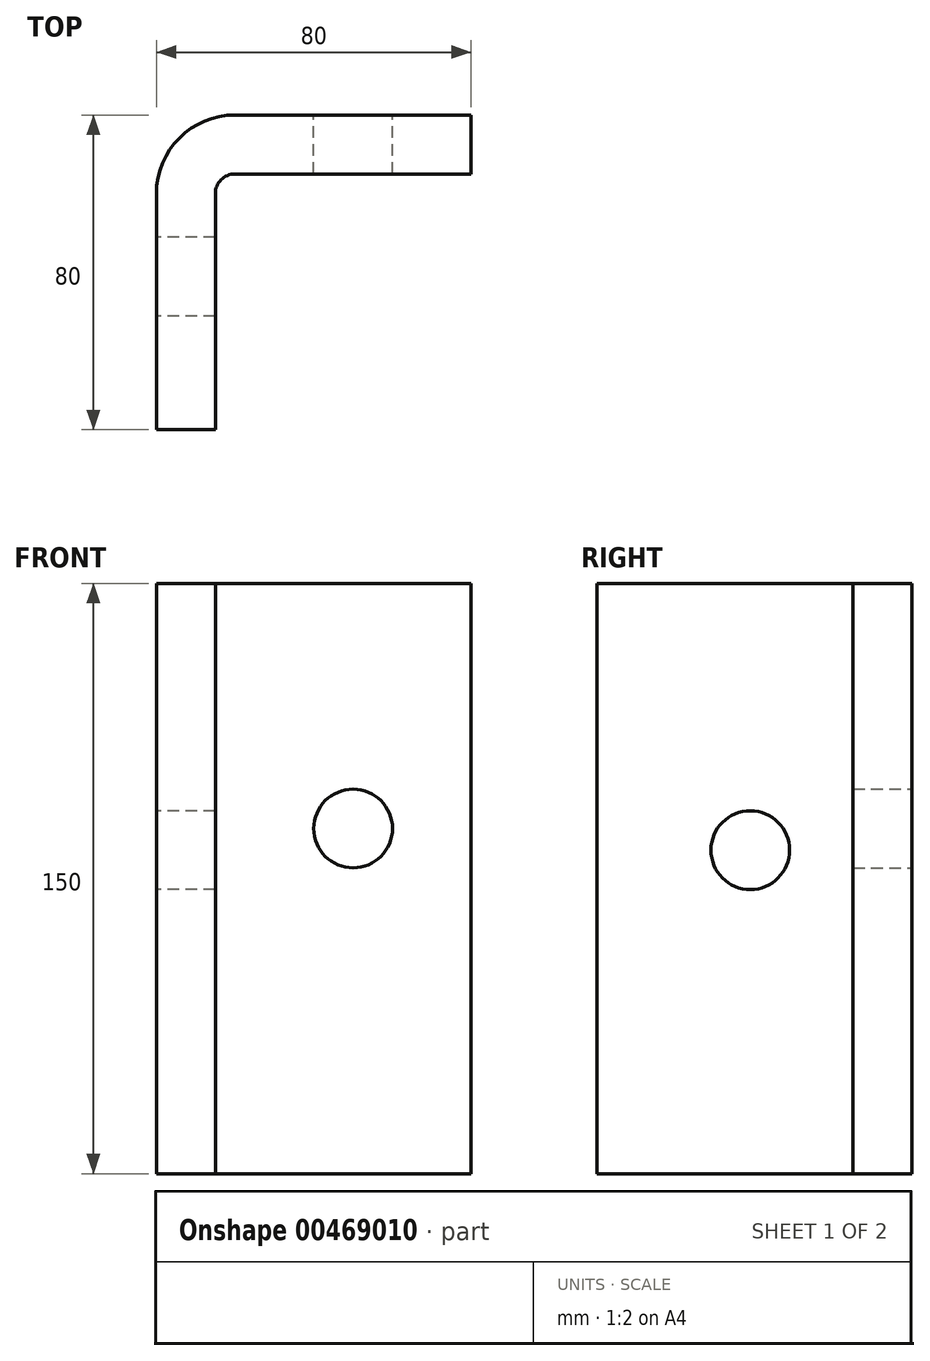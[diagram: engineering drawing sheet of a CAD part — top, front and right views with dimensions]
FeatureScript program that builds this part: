
annotation { "Feature Type Name" : "Feature", "Feature Type Description" : "" }
export const myFeature = defineFeature(function(context is Context, id is Id, definition is map)
    precondition{}
    {
        {
            var Q0;
            Q0=qCreatedBy(makeId("Top.planeOp"),FACE);
            var sketch = newSketch(context, id + "F0", { "sketchPlane" : qUnion([Q0])});
            skLineSegment(sketch, "E0", {"start": v(0, 0) * mm, "end": v(0, 80) * mm});
            skLineSegment(sketch, "E1", {"start": v(0, 80) * mm, "end": v(80, 80) * mm});
            skLineSegment(sketch, "E2", {"start": v(80, 80) * mm, "end": v(80, 65) * mm});
            skLineSegment(sketch, "E3", {"start": v(80, 65) * mm, "end": v(15, 65) * mm});
            skLineSegment(sketch, "E4", {"start": v(15, 65) * mm, "end": v(15, 0) * mm});
            skLineSegment(sketch, "E5", {"start": v(15, 0) * mm, "end": v(0, 0) * mm});
            skSolve(sketch);
        }
        {
            var Q0;
            Q0=makeQuery(id+"F0.imprint","IMPRINT",FACE,{"disambiguationData":[TD([[makeQuery(id+"F0.imprint","IMPRINT",EDGE,{"derivedFrom":sQuery(id+"F0.wireOp",EDGE,"E0")}),-1.0]])]});
            extrude(context, id + "F1", {"entities" : qUnion([Q0]), "depth" : 150 * mm});
        }
        {
            var Q0;
            Q0=makeQuery(id+"F1.opExtrude","SWEPT_EDGE",EDGE,{"disambiguationData":[OSD([sQuery(id+"F0.wireOp",EDGE,"E0"),sQuery(id+"F0.wireOp",EDGE,"E1")])]});
            fillet(context, id + "F2", {"entities" : qUnion([Q0]), "radius" : 20 * mm, "tangentPropagation" : true, "allowEdgeOverflow" : false});
        }
        {
            var Q0;
            Q0=makeQuery(id+"F1.opExtrude","SWEPT_EDGE",EDGE,{"disambiguationData":[OSD([sQuery(id+"F0.wireOp",EDGE,"E3"),sQuery(id+"F0.wireOp",EDGE,"E4")])]});
            fillet(context, id + "F3", {"entities" : qUnion([Q0]), "radius" : 5 * mm, "tangentPropagation" : true, "allowEdgeOverflow" : false});
        }
        {
            var Q0;
            Q0=makeQuery(id+"F1.opExtrude","SWEPT_FACE",FACE,{"disambiguationData":[OSD([sQuery(id+"F0.wireOp",EDGE,"E0")])]});
            var sketch = newSketch(context, id + "F4", { "sketchPlane" : qUnion([Q0])});
            skCircle(sketch, "E6", {"center": v(-38.9, 82.2) * mm, "radius": 10 * mm});
            skSolve(sketch);
        }
        {
            var Q0;
            Q0=makeQuery(id+"F4.imprint","IMPRINT",FACE,{"disambiguationData":[TD([[makeQuery(id+"F4.imprint","IMPRINT",EDGE,{"derivedFrom":sQuery(id+"F4.wireOp",EDGE,"E6")}),1.0]])]});
            extrude(context, id + "F5", {"entities" : qUnion([Q0]), "operationType" : NewBodyOperationType.REMOVE, "endBound" : BoundingType.THROUGH_ALL, "oppositeDirection" : true, "depth" : 25 * mm});
        }
        {
            var Q0;
            Q0=makeQuery(id+"F1.opExtrude","SWEPT_FACE",FACE,{"disambiguationData":[OSD([sQuery(id+"F0.wireOp",EDGE,"E1")])]});
            var sketch = newSketch(context, id + "F6", { "sketchPlane" : qUnion([Q0])});
            skCircle(sketch, "E7", {"center": v(-50, 87.69) * mm, "radius": 10 * mm});
            skPoint(sketch, "E7.centerSnap0", {"position": v(-50, 150) * mm});
            skSolve(sketch);
        }
        {
            var Q0;
            Q0=makeQuery(id+"F6.imprint","IMPRINT",FACE,{"disambiguationData":[TD([[makeQuery(id+"F6.imprint","IMPRINT",EDGE,{"derivedFrom":sQuery(id+"F6.wireOp",EDGE,"E7")}),1.0]])]});
            extrude(context, id + "F7", {"entities" : qUnion([Q0]), "operationType" : NewBodyOperationType.REMOVE, "endBound" : BoundingType.THROUGH_ALL, "oppositeDirection" : true, "depth" : 25 * mm});
        }
    });
